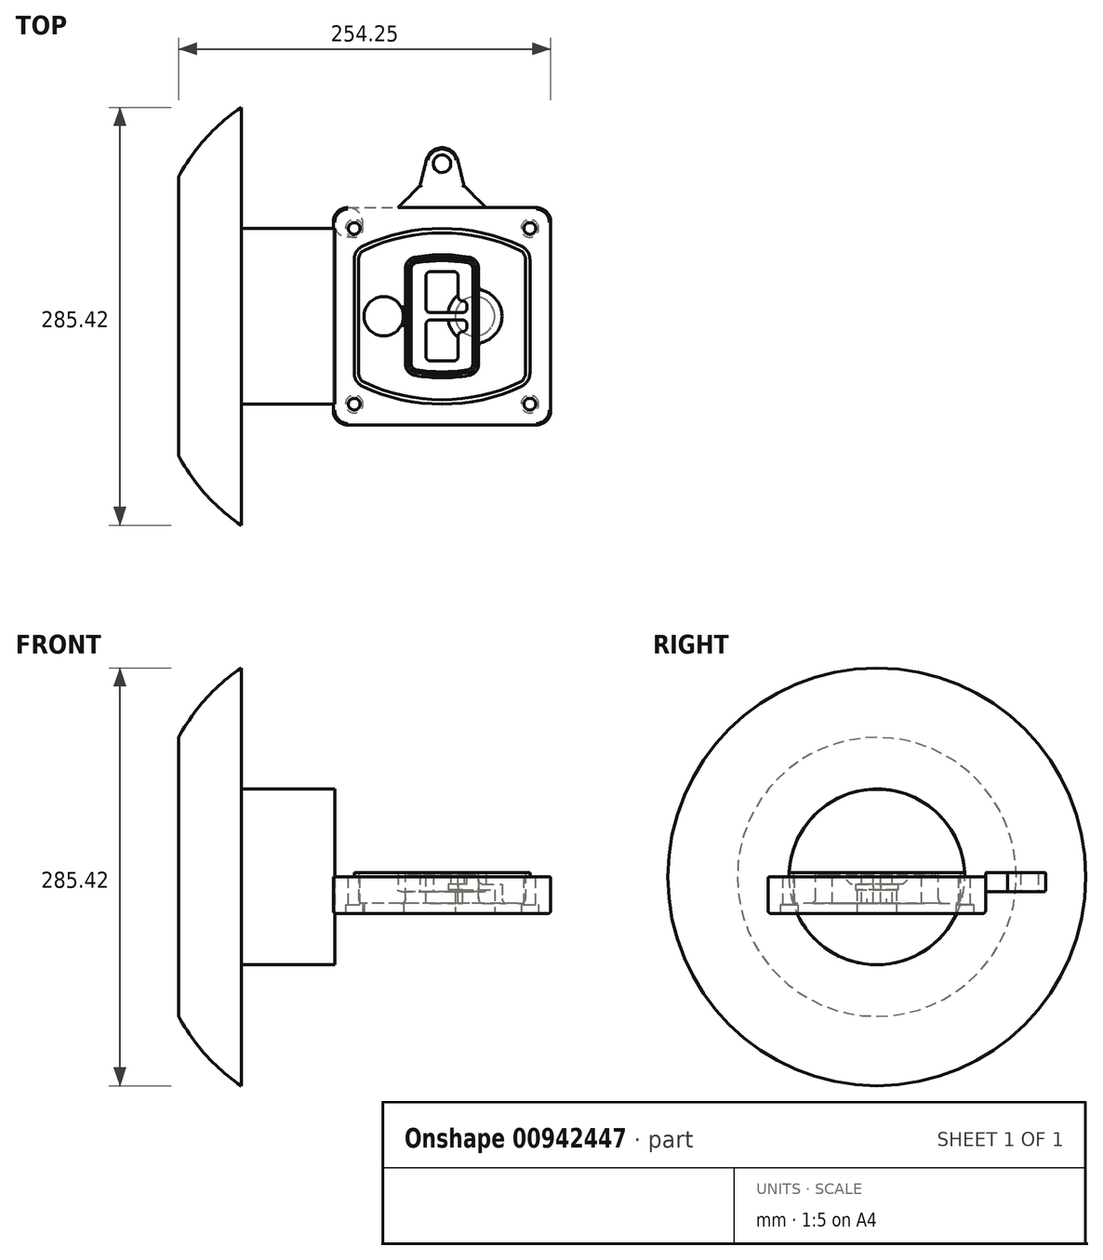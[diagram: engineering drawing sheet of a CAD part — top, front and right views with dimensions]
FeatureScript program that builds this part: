
annotation { "Feature Type Name" : "Feature", "Feature Type Description" : "" }
export const myFeature = defineFeature(function(context is Context, id is Id, definition is map)
    precondition{}
    {
        {
            var Q0;
            Q0=qCreatedBy(makeId("Top.planeOp"),FACE);
            var sketch = newSketch(context, id + "F0", { "sketchPlane" : qUnion([Q0])});
            skPoint(sketch, "E0.rect.middle", {"position": v(0, 0) * mm});
            skLineSegment(sketch, "E1.bottom", {"start": v(-64.25, -74.25) * mm, "end": v(64.25, -74.25) * mm});
            skLineSegment(sketch, "E1.top", {"start": v(-64.25, 74.25) * mm, "end": v(64.25, 74.25) * mm});
            skLineSegment(sketch, "E1.left", {"start": v(-74.25, -64.25) * mm, "end": v(-74.25, 64.25) * mm});
            skLineSegment(sketch, "E1.right", {"start": v(74.25, -64.25) * mm, "end": v(74.25, 64.25) * mm});
            skLineSegment(sketch, "E2", {"start": v(-74.25, 74.25) * mm, "end": v(74.25, -74.25) * mm, "construction": true});
            skLineSegment(sketch, "E3", {"start": v(74.25, 74.25) * mm, "end": v(-74.25, -74.25) * mm, "construction": true});
            skCircle(sketch, "E4", {"center": v(-60, 60) * mm, "radius": 4 * mm});
            skCircle(sketch, "E5", {"center": v(60, 60) * mm, "radius": 4 * mm});
            skCircle(sketch, "E6", {"center": v(60, -60) * mm, "radius": 4 * mm});
            skCircle(sketch, "E7", {"center": v(-60, -60) * mm, "radius": 4 * mm});
            skLineSegment(sketch, "E8", {"start": v(-60, 60) * mm, "end": v(60, 60) * mm, "construction": true});
            skLineSegment(sketch, "E9", {"start": v(60, 60) * mm, "end": v(60, -60) * mm, "construction": true});
            skLineSegment(sketch, "E10", {"start": v(60, -60) * mm, "end": v(-60, -60) * mm, "construction": true});
            skLineSegment(sketch, "E11", {"start": v(-60, -60) * mm, "end": v(-60, 60) * mm, "construction": true});
            skLineSegment(sketch, "E12", {"start": v(-60, 38.83) * mm, "end": v(-60, -38.83) * mm});
            skLineSegment(sketch, "E13", {"start": v(60, 38.83) * mm, "end": v(60, -38.83) * mm});
            skArc(sketch, "E14", {"start": v(54.26, 47.88) * mm, "mid": v(0, 60) * mm, "end": v(-54.26, 47.88) * mm});
            skArc(sketch, "E15", {"start": v(-54.26, -47.88) * mm, "mid": v(0, -60) * mm, "end": v(54.26, -47.88) * mm});
            skLineSegment(sketch, "E16", {"start": v(-60, 0) * mm, "end": v(60, 0) * mm, "construction": true});
            skPoint(sketch, "E17.visualSharp", {"position": v(-60, -45) * mm});
            skArc(sketch, "E17.filletArc", {"start": v(-60, -38.83) * mm, "mid": v(-58.44, -44.2) * mm, "end": v(-54.26, -47.88) * mm});
            skPoint(sketch, "E18.visualSharp", {"position": v(-60, 45) * mm});
            skArc(sketch, "E18.filletArc", {"start": v(-54.26, 47.88) * mm, "mid": v(-58.44, 44.2) * mm, "end": v(-60, 38.83) * mm});
            skPoint(sketch, "E19.visualSharp", {"position": v(60, 45) * mm});
            skArc(sketch, "E19.filletArc", {"start": v(60, 38.83) * mm, "mid": v(58.44, 44.2) * mm, "end": v(54.26, 47.88) * mm});
            skPoint(sketch, "E20.visualSharp", {"position": v(60, -45) * mm});
            skArc(sketch, "E20.filletArc", {"start": v(54.26, -47.88) * mm, "mid": v(58.44, -44.2) * mm, "end": v(60, -38.83) * mm});
            skPoint(sketch, "E21.visualSharp", {"position": v(-74.25, 74.25) * mm});
            skArc(sketch, "E21.filletArc", {"start": v(-64.25, 74.25) * mm, "mid": v(-71.32, 71.32) * mm, "end": v(-74.25, 64.25) * mm});
            skPoint(sketch, "E22.visualSharp", {"position": v(74.25, 74.25) * mm});
            skArc(sketch, "E22.filletArc", {"start": v(74.25, 64.25) * mm, "mid": v(71.32, 71.32) * mm, "end": v(64.25, 74.25) * mm});
            skPoint(sketch, "E23.visualSharp", {"position": v(74.25, -74.25) * mm});
            skArc(sketch, "E23.filletArc", {"start": v(64.25, -74.25) * mm, "mid": v(71.32, -71.32) * mm, "end": v(74.25, -64.25) * mm});
            skPoint(sketch, "E24.visualSharp", {"position": v(-74.25, -74.25) * mm});
            skArc(sketch, "E24.filletArc", {"start": v(-74.25, -64.25) * mm, "mid": v(-71.32, -71.32) * mm, "end": v(-64.25, -74.25) * mm});
            skArc(sketch, "E25.0", {"start": v(57, 38.83) * mm, "mid": v(55.9, 42.58) * mm, "end": v(52.98, 45.17) * mm});
            skLineSegment(sketch, "E25.1", {"start": v(57, 38.83) * mm, "end": v(57, -38.83) * mm});
            skArc(sketch, "E25.2", {"start": v(52.98, -45.17) * mm, "mid": v(55.9, -42.58) * mm, "end": v(57, -38.83) * mm});
            skArc(sketch, "E25.3", {"start": v(-52.98, -45.17) * mm, "mid": v(0, -57) * mm, "end": v(52.98, -45.17) * mm});
            skArc(sketch, "E25.4", {"start": v(-57, -38.83) * mm, "mid": v(-55.9, -42.58) * mm, "end": v(-52.98, -45.17) * mm});
            skArc(sketch, "E25.5", {"start": v(52.98, 45.17) * mm, "mid": v(0, 57) * mm, "end": v(-52.98, 45.17) * mm});
            skLineSegment(sketch, "E25.6", {"start": v(-57, 38.83) * mm, "end": v(-57, -38.83) * mm});
            skArc(sketch, "E25.7", {"start": v(-52.98, 45.17) * mm, "mid": v(-55.9, 42.58) * mm, "end": v(-57, 38.83) * mm});
            skArc(sketch, "E26.0", {"start": v(-55.96, 51.5) * mm, "mid": v(-61.82, 46.33) * mm, "end": v(-64, 38.83) * mm});
            skArc(sketch, "E26.1", {"start": v(55.96, 51.5) * mm, "mid": v(0, 64) * mm, "end": v(-55.96, 51.5) * mm});
            skArc(sketch, "E26.2", {"start": v(64, 38.83) * mm, "mid": v(61.82, 46.33) * mm, "end": v(55.96, 51.5) * mm});
            skLineSegment(sketch, "E26.3", {"start": v(64, 38.83) * mm, "end": v(64, -38.83) * mm});
            skArc(sketch, "E26.4", {"start": v(55.96, -51.5) * mm, "mid": v(61.82, -46.33) * mm, "end": v(64, -38.83) * mm});
            skLineSegment(sketch, "E26.5", {"start": v(-64, 38.83) * mm, "end": v(-64, -38.83) * mm});
            skArc(sketch, "E26.6", {"start": v(-55.96, -51.5) * mm, "mid": v(0, -64) * mm, "end": v(55.96, -51.5) * mm});
            skArc(sketch, "E26.7", {"start": v(-64, -38.83) * mm, "mid": v(-61.82, -46.33) * mm, "end": v(-55.96, -51.5) * mm});
            skSolve(sketch);
        }
        {
            var Q0;
            Q0=makeQuery(id+"F0.imprint","IMPRINT",FACE,{"disambiguationData":[TD([[makeQuery(id+"F0.imprint","IMPRINT",EDGE,{"derivedFrom":sQuery(id+"F0.wireOp",EDGE,"E1.bottom")}),1.0]])]});
            var Q1;
            Q1=makeQuery(id+"F0.imprint","IMPRINT",FACE,{"disambiguationData":[TD([[makeQuery(id+"F0.imprint","IMPRINT",EDGE,{"derivedFrom":sQuery(id+"F0.wireOp",EDGE,"E12")}),1.0]])]});
            var Q2;
            Q2=makeQuery(id+"F0.imprint","IMPRINT",FACE,{"disambiguationData":[TD([[makeQuery(id+"F0.imprint","IMPRINT",EDGE,{"derivedFrom":sQuery(id+"F0.wireOp",EDGE,"E25.0")}),1.0]])]});
            var Q3;
            Q3=makeQuery(id+"F0.imprint","IMPRINT",FACE,{"disambiguationData":[TD([[makeQuery(id+"F0.imprint","IMPRINT",EDGE,{"derivedFrom":sQuery(id+"F0.wireOp",EDGE,"E12")}),-1.0]])]});
            extrude(context, id + "F1", {"entities" : qUnion([Q0, Q1, Q2, Q3]), "oppositeDirection" : true, "depth" : 25 * mm});
        }
        {
            var Q0;
            Q0=makeQuery(id+"F0.imprint","IMPRINT",FACE,{"disambiguationData":[TD([[makeQuery(id+"F0.imprint","IMPRINT",EDGE,{"derivedFrom":sQuery(id+"F0.wireOp",EDGE,"E12")}),1.0]])]});
            extrude(context, id + "F2", {"entities" : qUnion([Q0]), "operationType" : NewBodyOperationType.ADD, "depth" : 3 * mm});
        }
        {
            var Q0;
            Q0=makeQuery(id+"F0.imprint","IMPRINT",FACE,{"disambiguationData":[TD([[makeQuery(id+"F0.imprint","IMPRINT",EDGE,{"derivedFrom":sQuery(id+"F0.wireOp",EDGE,"E25.0")}),1.0]])]});
            extrude(context, id + "F3", {"entities" : qUnion([Q0]), "operationType" : NewBodyOperationType.REMOVE, "oppositeDirection" : true, "depth" : 18 * mm});
        }
        {
            var Q0;
            Q0=makeQuery(id+"F2.opExtrude","CAP_FACE",FACE,{"disambiguationData":[OSD([sQuery(id+"F0.wireOp",EDGE,"E12"),sQuery(id+"F0.wireOp",EDGE,"E13"),sQuery(id+"F0.wireOp",EDGE,"E14"),sQuery(id+"F0.wireOp",EDGE,"E15"),sQuery(id+"F0.wireOp",EDGE,"E17.filletArc"),sQuery(id+"F0.wireOp",EDGE,"E18.filletArc"),sQuery(id+"F0.wireOp",EDGE,"E19.filletArc"),sQuery(id+"F0.wireOp",EDGE,"E20.filletArc"),sQuery(id+"F0.wireOp",EDGE,"E25.0"),sQuery(id+"F0.wireOp",EDGE,"E25.1"),sQuery(id+"F0.wireOp",EDGE,"E25.2"),sQuery(id+"F0.wireOp",EDGE,"E25.3"),sQuery(id+"F0.wireOp",EDGE,"E25.4"),sQuery(id+"F0.wireOp",EDGE,"E25.5"),sQuery(id+"F0.wireOp",EDGE,"E25.6"),sQuery(id+"F0.wireOp",EDGE,"E25.7")])],"isStart":false});
            var sketch = newSketch(context, id + "F4", { "sketchPlane" : qUnion([Q0])});
            skArc(sketch, "E27.0", {"start": v(-18.34, -40.45) * mm, "mid": v(0, -42) * mm, "end": v(18.34, -40.45) * mm});
            skArc(sketch, "E28.0", {"start": v(18.34, 40.45) * mm, "mid": v(0, 42) * mm, "end": v(-18.34, 40.45) * mm});
            skLineSegment(sketch, "E29", {"start": v(-25, 32.57) * mm, "end": v(-25, -32.57) * mm});
            skLineSegment(sketch, "E30", {"start": v(25, 32.57) * mm, "end": v(25, -32.57) * mm});
            skLineSegment(sketch, "E31", {"start": v(-25, 39.1) * mm, "end": v(25, 39.1) * mm, "construction": true});
            skLineSegment(sketch, "E32", {"start": v(-25, -39.1) * mm, "end": v(25, -39.1) * mm, "construction": true});
            skPoint(sketch, "E33.visualSharp", {"position": v(-25, 39.1) * mm});
            skArc(sketch, "E33.filletArc", {"start": v(-18.34, 40.45) * mm, "mid": v(-23.11, 37.73) * mm, "end": v(-25, 32.57) * mm});
            skPoint(sketch, "E34.visualSharp", {"position": v(25, 39.1) * mm});
            skArc(sketch, "E34.filletArc", {"start": v(25, 32.57) * mm, "mid": v(23.11, 37.73) * mm, "end": v(18.34, 40.45) * mm});
            skPoint(sketch, "E35.visualSharp", {"position": v(25, -39.1) * mm});
            skArc(sketch, "E35.filletArc", {"start": v(18.34, -40.45) * mm, "mid": v(23.11, -37.73) * mm, "end": v(25, -32.57) * mm});
            skPoint(sketch, "E36.visualSharp", {"position": v(-25, -39.1) * mm});
            skArc(sketch, "E36.filletArc", {"start": v(-25, -32.57) * mm, "mid": v(-23.11, -37.73) * mm, "end": v(-18.34, -40.45) * mm});
            skArc(sketch, "E37.0", {"start": v(52.98, 45.17) * mm, "mid": v(0, 57) * mm, "end": v(-52.98, 45.17) * mm});
            skArc(sketch, "E37.1", {"start": v(-52.98, 45.17) * mm, "mid": v(-55.9, 42.58) * mm, "end": v(-57, 38.83) * mm});
            skLineSegment(sketch, "E37.2", {"start": v(-57, 38.83) * mm, "end": v(-57, -38.83) * mm});
            skArc(sketch, "E37.3", {"start": v(-57, -38.83) * mm, "mid": v(-55.9, -42.58) * mm, "end": v(-52.98, -45.17) * mm});
            skArc(sketch, "E37.4", {"start": v(-52.98, -45.17) * mm, "mid": v(0, -57) * mm, "end": v(52.98, -45.17) * mm});
            skArc(sketch, "E37.5", {"start": v(52.98, -45.17) * mm, "mid": v(55.9, -42.58) * mm, "end": v(57, -38.83) * mm});
            skLineSegment(sketch, "E37.6", {"start": v(57, 38.83) * mm, "end": v(57, -38.83) * mm});
            skArc(sketch, "E37.7", {"start": v(57, 38.83) * mm, "mid": v(55.9, 42.58) * mm, "end": v(52.98, 45.17) * mm});
            skLineSegment(sketch, "E38.0", {"start": v(23, 32.57) * mm, "end": v(23, -32.57) * mm});
            skArc(sketch, "E38.1", {"start": v(18, -38.48) * mm, "mid": v(21.58, -36.44) * mm, "end": v(23, -32.57) * mm});
            skArc(sketch, "E38.2", {"start": v(-18, -38.48) * mm, "mid": v(0, -40) * mm, "end": v(18, -38.48) * mm});
            skArc(sketch, "E38.3", {"start": v(-23, -32.57) * mm, "mid": v(-21.58, -36.44) * mm, "end": v(-18, -38.48) * mm});
            skLineSegment(sketch, "E38.4", {"start": v(-23, 32.57) * mm, "end": v(-23, -32.57) * mm});
            skArc(sketch, "E38.5", {"start": v(23, 32.57) * mm, "mid": v(21.58, 36.44) * mm, "end": v(18, 38.48) * mm});
            skArc(sketch, "E38.6", {"start": v(-18, 38.48) * mm, "mid": v(-21.58, 36.44) * mm, "end": v(-23, 32.57) * mm});
            skArc(sketch, "E38.7", {"start": v(18, 38.48) * mm, "mid": v(0, 40) * mm, "end": v(-18, 38.48) * mm});
            skArc(sketch, "E39.0", {"start": v(21, 32.57) * mm, "mid": v(20.06, 35.15) * mm, "end": v(17.67, 36.5) * mm});
            skLineSegment(sketch, "E39.1", {"start": v(21, 32.57) * mm, "end": v(21, -32.57) * mm});
            skArc(sketch, "E39.2", {"start": v(17.67, -36.5) * mm, "mid": v(20.06, -35.15) * mm, "end": v(21, -32.57) * mm});
            skArc(sketch, "E39.3", {"start": v(-17.67, -36.5) * mm, "mid": v(0, -38) * mm, "end": v(17.67, -36.5) * mm});
            skArc(sketch, "E39.4", {"start": v(-21, -32.57) * mm, "mid": v(-20.06, -35.15) * mm, "end": v(-17.67, -36.5) * mm});
            skArc(sketch, "E39.5", {"start": v(17.67, 36.5) * mm, "mid": v(0, 38) * mm, "end": v(-17.67, 36.5) * mm});
            skLineSegment(sketch, "E39.6", {"start": v(-21, 32.57) * mm, "end": v(-21, -32.57) * mm});
            skArc(sketch, "E39.7", {"start": v(-17.67, 36.5) * mm, "mid": v(-20.06, 35.15) * mm, "end": v(-21, 32.57) * mm});
            skLineSegment(sketch, "E40", {"start": v(-25, 0) * mm, "end": v(25, 0) * mm, "construction": true});
            skLineSegment(sketch, "E41", {"start": v(-11, 5.5) * mm, "end": v(-11, 27.5) * mm});
            skLineSegment(sketch, "E42", {"start": v(-8, 30.5) * mm, "end": v(8, 30.5) * mm});
            skLineSegment(sketch, "E43", {"start": v(11, 27.5) * mm, "end": v(11, 13.5) * mm});
            skLineSegment(sketch, "E44", {"start": v(14, 10.5) * mm, "end": v(14, 10.5) * mm});
            skLineSegment(sketch, "E45", {"start": v(17, 7.5) * mm, "end": v(17, 5.5) * mm});
            skLineSegment(sketch, "E46", {"start": v(14, 2.5) * mm, "end": v(-8, 2.5) * mm});
            skPoint(sketch, "E47.visualSharp", {"position": v(-11, 30.5) * mm});
            skArc(sketch, "E47.filletArc", {"start": v(-8, 30.5) * mm, "mid": v(-10.12, 29.62) * mm, "end": v(-11, 27.5) * mm});
            skPoint(sketch, "E48.visualSharp", {"position": v(11, 30.5) * mm});
            skArc(sketch, "E48.filletArc", {"start": v(11, 27.5) * mm, "mid": v(10.12, 29.62) * mm, "end": v(8, 30.5) * mm});
            skPoint(sketch, "E49.visualSharp", {"position": v(11, 10.5) * mm});
            skArc(sketch, "E49.filletArc", {"start": v(11, 13.5) * mm, "mid": v(11.88, 11.38) * mm, "end": v(14, 10.5) * mm});
            skPoint(sketch, "E50.visualSharp", {"position": v(17, 10.5) * mm});
            skArc(sketch, "E50.filletArc", {"start": v(17, 7.5) * mm, "mid": v(16.12, 9.62) * mm, "end": v(14, 10.5) * mm});
            skPoint(sketch, "E51.visualSharp", {"position": v(17, 2.5) * mm});
            skArc(sketch, "E51.filletArc", {"start": v(14, 2.5) * mm, "mid": v(16.12, 3.38) * mm, "end": v(17, 5.5) * mm});
            skPoint(sketch, "E52.visualSharp", {"position": v(-11, 2.5) * mm});
            skArc(sketch, "E52.filletArc", {"start": v(-11, 5.5) * mm, "mid": v(-10.12, 3.38) * mm, "end": v(-8, 2.5) * mm});
            skLineSegment(sketch, "E53.0.MirrorCS", {"start": v(14, -2.5) * mm, "end": v(-8, -2.5) * mm});
            skArc(sketch, "E54.0.MirrorCS", {"start": v(-11, -5.5) * mm, "mid": v(-10.12, -3.38) * mm, "end": v(-8, -2.5) * mm});
            skLineSegment(sketch, "E55.0.MirrorCS", {"start": v(-11, -5.5) * mm, "end": v(-11, -27.5) * mm});
            skArc(sketch, "E56.0.MirrorCS", {"start": v(-8, -30.5) * mm, "mid": v(-10.12, -29.62) * mm, "end": v(-11, -27.5) * mm});
            skLineSegment(sketch, "E57.0.MirrorCS", {"start": v(-8, -30.5) * mm, "end": v(8, -30.5) * mm});
            skArc(sketch, "E58.0.MirrorCS", {"start": v(11, -27.5) * mm, "mid": v(10.12, -29.62) * mm, "end": v(8, -30.5) * mm});
            skLineSegment(sketch, "E59.0.MirrorCS", {"start": v(11, -27.5) * mm, "end": v(11, -13.5) * mm});
            skArc(sketch, "E60.0.MirrorCS", {"start": v(11, -13.5) * mm, "mid": v(11.88, -11.38) * mm, "end": v(14, -10.5) * mm});
            skArc(sketch, "E61.0.MirrorCS", {"start": v(17, -7.5) * mm, "mid": v(16.12, -9.62) * mm, "end": v(14, -10.5) * mm});
            skLineSegment(sketch, "E62.0.MirrorCS", {"start": v(17, -7.5) * mm, "end": v(17, -5.5) * mm});
            skArc(sketch, "E63.0.MirrorCS", {"start": v(14, -2.5) * mm, "mid": v(16.12, -3.38) * mm, "end": v(17, -5.5) * mm});
            skSolve(sketch);
        }
        {
            var Q0;
            Q0=makeQuery(id+"F4.imprint","IMPRINT",FACE,{"disambiguationData":[TD([[makeQuery(id+"F4.imprint","IMPRINT",EDGE,{"derivedFrom":sQuery(id+"F4.wireOp",EDGE,"E27.0")}),1.0]])]});
            var Q1;
            Q1=makeQuery(id+"F4.imprint","IMPRINT",FACE,{"disambiguationData":[TD([[makeQuery(id+"F4.imprint","IMPRINT",EDGE,{"derivedFrom":sQuery(id+"F4.wireOp",EDGE,"E38.0")}),-1.0]])]});
            var Q2;
            Q2=makeQuery(id+"F4.imprint","IMPRINT",FACE,{"disambiguationData":[TD([[makeQuery(id+"F4.imprint","IMPRINT",EDGE,{"derivedFrom":sQuery(id+"F4.wireOp",EDGE,"E39.0")}),1.0]])]});
            extrude(context, id + "F5", {"entities" : qUnion([Q0, Q1, Q2]), "operationType" : NewBodyOperationType.ADD, "endBound" : BoundingType.UP_TO_NEXT, "oppositeDirection" : true, "depth" : 25 * mm});
        }
        {
            var Q0;
            Q0=makeQuery(id+"F4.imprint","IMPRINT",FACE,{"disambiguationData":[TD([[makeQuery(id+"F4.imprint","IMPRINT",EDGE,{"derivedFrom":sQuery(id+"F4.wireOp",EDGE,"E38.0")}),-1.0]])]});
            extrude(context, id + "F6", {"entities" : qUnion([Q0]), "operationType" : NewBodyOperationType.REMOVE, "oppositeDirection" : true, "depth" : 2 * mm});
        }
        {
            var Q0;
            Q0=makeQuery(id+"F1.opExtrude","CAP_FACE",FACE,{"disambiguationData":[OSD([sQuery(id+"F0.wireOp",EDGE,"E1.bottom"),sQuery(id+"F0.wireOp",EDGE,"E1.top"),sQuery(id+"F0.wireOp",EDGE,"E1.left"),sQuery(id+"F0.wireOp",EDGE,"E1.right"),sQuery(id+"F0.wireOp",EDGE,"E4"),sQuery(id+"F0.wireOp",EDGE,"E5"),sQuery(id+"F0.wireOp",EDGE,"E6"),sQuery(id+"F0.wireOp",EDGE,"E7"),sQuery(id+"F0.wireOp",EDGE,"E21.filletArc"),sQuery(id+"F0.wireOp",EDGE,"E22.filletArc"),sQuery(id+"F0.wireOp",EDGE,"E23.filletArc"),sQuery(id+"F0.wireOp",EDGE,"E24.filletArc")])],"isStart":false});
            var sketch = newSketch(context, id + "F7", { "sketchPlane" : qUnion([Q0])});
            skCircle(sketch, "E64", {"center": v(22.5, 0) * mm, "radius": 13.47 * mm});
            skCircle(sketch, "E65", {"center": v(-39.81, 0) * mm, "radius": 13.47 * mm});
            skLineSegment(sketch, "E66", {"start": v(74.25, 0) * mm, "end": v(-74.25, 0) * mm});
            skCircle(sketch, "E67", {"center": v(22.5, 0) * mm, "radius": 18.47 * mm});
            skCircle(sketch, "E68", {"center": v(60, -60) * mm, "radius": 6 * mm});
            skCircle(sketch, "E69", {"center": v(-60, -60) * mm, "radius": 6 * mm});
            skCircle(sketch, "E70", {"center": v(-60, 60) * mm, "radius": 6 * mm});
            skCircle(sketch, "E71", {"center": v(60, 60) * mm, "radius": 6 * mm});
            skSolve(sketch);
        }
        {
            var Q0;
            {var subQ1=sQuery(id+"F7.wireOp",EDGE,"E66");var subQ4=sQuery(id+"F7.wireOp",EDGE,"E64");var subQ6=makeQuery(id+"F7.imprint","INTERSECT",VERTEX,{"disambiguationData":[OD(0.0)],"derivedFrom":[subQ4,subQ1]});Q0=makeQuery(id+"F7.imprint","IMPRINT",FACE,{"disambiguationData":[TD([[makeQuery(id+"F7.imprint","IMPRINT",EDGE,{"disambiguationData":[TD([[subQ6,-1.0]])],"derivedFrom":subQ4}),-1.0]])]});}
            var Q1;
            {var subQ0=sQuery(id+"F7.wireOp",EDGE,"E66");var subQ1=sQuery(id+"F7.wireOp",EDGE,"E64");var subQ3=makeQuery(id+"F7.imprint","INTERSECT",VERTEX,{"disambiguationData":[OD(0.0)],"derivedFrom":[subQ1,subQ0]});Q1=makeQuery(id+"F7.imprint","IMPRINT",FACE,{"disambiguationData":[TD([[makeQuery(id+"F7.imprint","IMPRINT",EDGE,{"disambiguationData":[TD([[subQ3,-1.0]])],"derivedFrom":subQ1}),1.0]])]});}
            var Q2;
            {var subQ0=sQuery(id+"F7.wireOp",EDGE,"E66");var subQ1=sQuery(id+"F7.wireOp",EDGE,"E64");var subQ3=makeQuery(id+"F7.imprint","INTERSECT",VERTEX,{"disambiguationData":[OD(0.0)],"derivedFrom":[subQ1,subQ0]});Q2=makeQuery(id+"F7.imprint","IMPRINT",FACE,{"disambiguationData":[TD([[makeQuery(id+"F7.imprint","IMPRINT",EDGE,{"disambiguationData":[TD([[subQ3,1.0]])],"derivedFrom":subQ1}),1.0]])]});}
            var Q3;
            {var subQ1=sQuery(id+"F7.wireOp",EDGE,"E66");var subQ4=sQuery(id+"F7.wireOp",EDGE,"E64");var subQ6=makeQuery(id+"F7.imprint","INTERSECT",VERTEX,{"disambiguationData":[OD(0.0)],"derivedFrom":[subQ4,subQ1]});Q3=makeQuery(id+"F7.imprint","IMPRINT",FACE,{"disambiguationData":[TD([[makeQuery(id+"F7.imprint","IMPRINT",EDGE,{"disambiguationData":[TD([[subQ6,1.0]])],"derivedFrom":subQ4}),-1.0]])]});}
            extrude(context, id + "F8", {"entities" : qUnion([Q0, Q1, Q2, Q3]), "operationType" : NewBodyOperationType.ADD, "oppositeDirection" : true, "depth" : 20 * mm});
        }
        {
            var Q0;
            {var subQ0=sQuery(id+"F7.wireOp",EDGE,"E66");var subQ1=sQuery(id+"F7.wireOp",EDGE,"E64");var subQ3=makeQuery(id+"F7.imprint","INTERSECT",VERTEX,{"disambiguationData":[OD(0.0)],"derivedFrom":[subQ1,subQ0]});Q0=makeQuery(id+"F7.imprint","IMPRINT",FACE,{"disambiguationData":[TD([[makeQuery(id+"F7.imprint","IMPRINT",EDGE,{"disambiguationData":[TD([[subQ3,-1.0]])],"derivedFrom":subQ1}),1.0]])]});}
            var Q1;
            {var subQ0=sQuery(id+"F7.wireOp",EDGE,"E66");var subQ1=sQuery(id+"F7.wireOp",EDGE,"E64");var subQ3=makeQuery(id+"F7.imprint","INTERSECT",VERTEX,{"disambiguationData":[OD(0.0)],"derivedFrom":[subQ1,subQ0]});Q1=makeQuery(id+"F7.imprint","IMPRINT",FACE,{"disambiguationData":[TD([[makeQuery(id+"F7.imprint","IMPRINT",EDGE,{"disambiguationData":[TD([[subQ3,1.0]])],"derivedFrom":subQ1}),1.0]])]});}
            extrude(context, id + "F9", {"entities" : qUnion([Q0, Q1]), "operationType" : NewBodyOperationType.REMOVE, "oppositeDirection" : true, "depth" : 16 * mm});
        }
        {
            var Q0;
            {var subQ0=sQuery(id+"F7.wireOp",EDGE,"E66");var subQ1=sQuery(id+"F7.wireOp",EDGE,"E65");var subQ3=makeQuery(id+"F7.imprint","INTERSECT",VERTEX,{"disambiguationData":[OD(0.0)],"derivedFrom":[subQ1,subQ0]});Q0=makeQuery(id+"F7.imprint","IMPRINT",FACE,{"disambiguationData":[TD([[makeQuery(id+"F7.imprint","IMPRINT",EDGE,{"disambiguationData":[TD([[subQ3,-1.0]])],"derivedFrom":subQ1}),1.0]])]});}
            var Q1;
            {var subQ0=sQuery(id+"F7.wireOp",EDGE,"E66");var subQ1=sQuery(id+"F7.wireOp",EDGE,"E65");var subQ3=makeQuery(id+"F7.imprint","INTERSECT",VERTEX,{"disambiguationData":[OD(0.0)],"derivedFrom":[subQ1,subQ0]});Q1=makeQuery(id+"F7.imprint","IMPRINT",FACE,{"disambiguationData":[TD([[makeQuery(id+"F7.imprint","IMPRINT",EDGE,{"disambiguationData":[TD([[subQ3,1.0]])],"derivedFrom":subQ1}),1.0]])]});}
            extrude(context, id + "F10", {"entities" : qUnion([Q0, Q1]), "operationType" : NewBodyOperationType.REMOVE, "oppositeDirection" : true, "depth" : 25 * mm});
        }
        {
            var Q0;
            Q0=makeQuery(id+"F7.imprint","IMPRINT",FACE,{"disambiguationData":[TD([[makeQuery(id+"F7.imprint","IMPRINT",EDGE,{"derivedFrom":sQuery(id+"F7.wireOp",EDGE,"E68")}),1.0]])]});
            var Q1;
            Q1=makeQuery(id+"F7.imprint","IMPRINT",FACE,{"disambiguationData":[TD([[makeQuery(id+"F7.imprint","IMPRINT",EDGE,{"derivedFrom":makeQuery(id+"F1.opExtrude","CAP_EDGE",EDGE,{"disambiguationData":[OSD([sQuery(id+"F0.wireOp",EDGE,"E5")])],"isStart":false})}),-1.0]])]});
            var Q2;
            Q2=makeQuery(id+"F7.imprint","IMPRINT",FACE,{"disambiguationData":[TD([[makeQuery(id+"F7.imprint","IMPRINT",EDGE,{"derivedFrom":sQuery(id+"F7.wireOp",EDGE,"E69")}),1.0]])]});
            var Q3;
            Q3=makeQuery(id+"F7.imprint","IMPRINT",FACE,{"disambiguationData":[TD([[makeQuery(id+"F7.imprint","IMPRINT",EDGE,{"derivedFrom":makeQuery(id+"F1.opExtrude","CAP_EDGE",EDGE,{"disambiguationData":[OSD([sQuery(id+"F0.wireOp",EDGE,"E4")])],"isStart":false})}),-1.0]])]});
            var Q4;
            Q4=makeQuery(id+"F7.imprint","IMPRINT",FACE,{"disambiguationData":[TD([[makeQuery(id+"F7.imprint","IMPRINT",EDGE,{"derivedFrom":sQuery(id+"F7.wireOp",EDGE,"E70")}),1.0]])]});
            var Q5;
            Q5=makeQuery(id+"F7.imprint","IMPRINT",FACE,{"disambiguationData":[TD([[makeQuery(id+"F7.imprint","IMPRINT",EDGE,{"derivedFrom":makeQuery(id+"F1.opExtrude","CAP_EDGE",EDGE,{"disambiguationData":[OSD([sQuery(id+"F0.wireOp",EDGE,"E7")])],"isStart":false})}),-1.0]])]});
            var Q6;
            Q6=makeQuery(id+"F7.imprint","IMPRINT",FACE,{"disambiguationData":[TD([[makeQuery(id+"F7.imprint","IMPRINT",EDGE,{"derivedFrom":sQuery(id+"F7.wireOp",EDGE,"E71")}),1.0]])]});
            var Q7;
            Q7=makeQuery(id+"F7.imprint","IMPRINT",FACE,{"disambiguationData":[TD([[makeQuery(id+"F7.imprint","IMPRINT",EDGE,{"derivedFrom":makeQuery(id+"F1.opExtrude","CAP_EDGE",EDGE,{"disambiguationData":[OSD([sQuery(id+"F0.wireOp",EDGE,"E6")])],"isStart":false})}),-1.0]])]});
            extrude(context, id + "F11", {"entities" : qUnion([Q0, Q1, Q2, Q3, Q4, Q5, Q6, Q7]), "operationType" : NewBodyOperationType.REMOVE, "oppositeDirection" : true, "depth" : 6 * mm});
        }
        {
            var Q0;
            Q0=makeQuery(id+"F9.boolean.opBoolean","COPY",FACE,{"derivedFrom":makeQuery(id+"F9.opExtrude","CAP_FACE",FACE,{"disambiguationData":[OSD([sQuery(id+"F7.wireOp",EDGE,"E64")])],"isStart":false})});
            var sketch = newSketch(context, id + "F12", { "sketchPlane" : qUnion([Q0])});
            skArc(sketch, "E72.0", {"start": v(11, 14.45) * mm, "mid": v(6.45, 9.13) * mm, "end": v(4.2, 2.5) * mm});
            skArc(sketch, "E72.1", {"start": v(4.2, -2.5) * mm, "mid": v(6.45, -9.13) * mm, "end": v(11, -14.45) * mm});
            skLineSegment(sketch, "E73", {"start": v(4.2, -2.5) * mm, "end": v(14, -2.5) * mm});
            skLineSegment(sketch, "E74.0", {"start": v(14, 2.5) * mm, "end": v(4.2, 2.5) * mm});
            skArc(sketch, "E74.1", {"start": v(14, 2.5) * mm, "mid": v(16.12, 3.38) * mm, "end": v(17, 5.5) * mm});
            skLineSegment(sketch, "E74.2", {"start": v(17, 7.5) * mm, "end": v(17, 5.5) * mm});
            skArc(sketch, "E74.3", {"start": v(17, 7.5) * mm, "mid": v(16.12, 9.62) * mm, "end": v(14, 10.5) * mm});
            skArc(sketch, "E74.4", {"start": v(11, 13.5) * mm, "mid": v(11.88, 11.38) * mm, "end": v(14, 10.5) * mm});
            skLineSegment(sketch, "E74.5", {"start": v(11, 14.45) * mm, "end": v(11, 13.5) * mm});
            skLineSegment(sketch, "E74.7", {"start": v(14, -2.5) * mm, "end": v(4.2, -2.5) * mm});
            skArc(sketch, "E74.8", {"start": v(14, -2.5) * mm, "mid": v(16.12, -3.38) * mm, "end": v(17, -5.5) * mm});
            skLineSegment(sketch, "E74.9", {"start": v(17, -7.5) * mm, "end": v(17, -5.5) * mm});
            skArc(sketch, "E74.10", {"start": v(17, -7.5) * mm, "mid": v(16.12, -9.62) * mm, "end": v(14, -10.5) * mm});
            skArc(sketch, "E74.11", {"start": v(11, -13.5) * mm, "mid": v(11.88, -11.38) * mm, "end": v(14, -10.5) * mm});
            skLineSegment(sketch, "E74.12", {"start": v(11, -14.45) * mm, "end": v(11, -13.5) * mm});
            skPoint(sketch, "E75.orphan", {"position": v(11, -27.5) * mm});
            skPoint(sketch, "E76.orphan", {"position": v(-8, -2.5) * mm});
            skPoint(sketch, "E77.orphan", {"position": v(-8, 2.5) * mm});
            skPoint(sketch, "E78.orphan", {"position": v(11, 27.5) * mm});
            skSolve(sketch);
        }
        {
            var Q0;
            {var subQ7=sQuery(id+"F12.wireOp",EDGE,"E72.0");var subQ14=sQuery(id+"F12.wireOp",EDGE,"E72.1");var subQ16=sQuery(id+"F12.wireOp",EDGE,"E74.1");var subQ18=sQuery(id+"F12.wireOp",EDGE,"E74.8");Q0=qUnion([makeQuery(id+"F12.imprint","IMPRINT",FACE,{"disambiguationData":[TD([[makeQuery(id+"F12.imprint","IMPRINT",EDGE,{"derivedFrom":subQ7}),1.0]])]}),makeQuery(id+"F12.imprint","IMPRINT",FACE,{"disambiguationData":[TD([[makeQuery(id+"F12.imprint","IMPRINT",EDGE,{"derivedFrom":subQ14}),1.0]])]}),makeQuery(id+"F12.imprint","IMPRINT",FACE,{"disambiguationData":[TD([[makeQuery(id+"F12.imprint","IMPRINT",EDGE,{"derivedFrom":subQ16}),1.0]])]}),makeQuery(id+"F12.imprint","IMPRINT",FACE,{"disambiguationData":[TD([[makeQuery(id+"F12.imprint","IMPRINT",EDGE,{"derivedFrom":subQ18}),-1.0]])]})]);}
            var Q1;
            Q1=makeQuery(id+"F5.boolean.opBoolean","SPLIT",FACE,{"disambiguationData":[TD([makeQuery(id+"F5.opExtrude","SWEPT_FACE",FACE,{"disambiguationData":[OSD([sQuery(id+"F4.wireOp",EDGE,"E41")])]})])],"derivedFrom":makeQuery(id+"F3.boolean.opBoolean","COPY",FACE,{"derivedFrom":makeQuery(id+"F3.opExtrude","CAP_FACE",FACE,{"disambiguationData":[OSD([sQuery(id+"F0.wireOp",EDGE,"E25.0"),sQuery(id+"F0.wireOp",EDGE,"E25.1"),sQuery(id+"F0.wireOp",EDGE,"E25.2"),sQuery(id+"F0.wireOp",EDGE,"E25.3"),sQuery(id+"F0.wireOp",EDGE,"E25.4"),sQuery(id+"F0.wireOp",EDGE,"E25.5"),sQuery(id+"F0.wireOp",EDGE,"E25.6"),sQuery(id+"F0.wireOp",EDGE,"E25.7")])],"isStart":false})})});
            extrude(context, id + "F13", {"entities" : qUnion([Q0]), "operationType" : NewBodyOperationType.REMOVE, "endBound" : BoundingType.UP_TO_SURFACE, "endBoundEntityFace" : qUnion([Q1]), "depth" : 25 * mm});
        }
        {
            var Q0;
            Q0=makeQuery(id+"F3.boolean.opBoolean","COPY",EDGE,{"derivedFrom":makeQuery(id+"F3.opExtrude","CAP_EDGE",EDGE,{"disambiguationData":[OSD([sQuery(id+"F0.wireOp",EDGE,"E25.6")])],"isStart":false})});
            var Q1;
            Q1=makeQuery(id+"F8.boolean.opBoolean","INTERSECT",EDGE,{"derivedFrom":[makeQuery(id+"F5.opExtrude","SWEPT_FACE",FACE,{"disambiguationData":[OSD([sQuery(id+"F4.wireOp",EDGE,"E30")])]}),makeQuery(id+"F8.opExtrude","CAP_FACE",FACE,{"disambiguationData":[OSD([sQuery(id+"F7.wireOp",EDGE,"E67")])],"isStart":false})]});
            var Q2;
            Q2=makeQuery(id+"F8.boolean.opBoolean","INTERSECT",EDGE,{"disambiguationData":[OD(1.0)],"derivedFrom":[makeQuery(id+"F5.opExtrude","SWEPT_FACE",FACE,{"disambiguationData":[OSD([sQuery(id+"F4.wireOp",EDGE,"E30")])]}),makeQuery(id+"F8.opExtrude","SWEPT_FACE",FACE,{"disambiguationData":[OSD([sQuery(id+"F7.wireOp",EDGE,"E67")])]})]});
            var Q3;
            {var subQ0=sQuery(id+"F4.wireOp",EDGE,"E30");Q3=makeQuery(id+"F8.boolean.opBoolean","SPLIT",EDGE,{"disambiguationData":[TD([makeQuery(id+"F5.opExtrude","SWEPT_FACE",FACE,{"disambiguationData":[OSD([sQuery(id+"F4.wireOp",EDGE,"E35.filletArc")])]})])],"derivedFrom":makeQuery(id+"F5.opExtrude","CAP_EDGE",EDGE,{"disambiguationData":[OSD([subQ0])],"isStart":false})});}
            var Q4;
            {var subQ0=sQuery(id+"F0.wireOp",EDGE,"E25.7");var subQ1=sQuery(id+"F0.wireOp",EDGE,"E25.1");var subQ2=sQuery(id+"F0.wireOp",EDGE,"E25.6");var subQ3=sQuery(id+"F0.wireOp",EDGE,"E25.5");var subQ4=sQuery(id+"F0.wireOp",EDGE,"E25.4");var subQ5=sQuery(id+"F0.wireOp",EDGE,"E25.0");var subQ6=sQuery(id+"F0.wireOp",EDGE,"E25.2");var subQ7=sQuery(id+"F0.wireOp",EDGE,"E25.3");Q4=makeQuery(id+"F8.boolean.opBoolean","INTERSECT",EDGE,{"derivedFrom":[makeQuery(id+"F5.boolean.opBoolean","SPLIT",FACE,{"disambiguationData":[TD([makeQuery(id+"F2.opExtrude","SWEPT_FACE",FACE,{"disambiguationData":[OSD([subQ5])]})])],"derivedFrom":makeQuery(id+"F3.boolean.opBoolean","COPY",FACE,{"derivedFrom":makeQuery(id+"F3.opExtrude","CAP_FACE",FACE,{"disambiguationData":[OSD([subQ5,subQ1,subQ6,subQ7,subQ4,subQ3,subQ2,subQ0])],"isStart":false})})}),makeQuery(id+"F8.opExtrude","SWEPT_FACE",FACE,{"disambiguationData":[OSD([sQuery(id+"F7.wireOp",EDGE,"E67")])]})]});}
            var Q5;
            Q5=makeQuery(id+"F8.boolean.opBoolean","INTERSECT",EDGE,{"disambiguationData":[OD(0.0)],"derivedFrom":[makeQuery(id+"F5.opExtrude","SWEPT_FACE",FACE,{"disambiguationData":[OSD([sQuery(id+"F4.wireOp",EDGE,"E30")])]}),makeQuery(id+"F8.opExtrude","SWEPT_FACE",FACE,{"disambiguationData":[OSD([sQuery(id+"F7.wireOp",EDGE,"E67")])]})]});
            fillet(context, id + "F14", {"entities" : qUnion([Q0, Q1, Q2, Q3, Q4, Q5]), "radius" : 3 * mm, "tangentPropagation" : true, "allowEdgeOverflow" : false});
        }
        {
            var Q0;
            Q0=makeQuery(id+"F1.opExtrude","CAP_EDGE",EDGE,{"disambiguationData":[OSD([sQuery(id+"F0.wireOp",EDGE,"E1.bottom")])],"isStart":false});
            fillet(context, id + "F15", {"entities" : qUnion([Q0]), "radius" : 2 * mm, "tangentPropagation" : true, "allowEdgeOverflow" : false});
        }
        {
            var Q0;
            {var subQ0=sQuery(id+"F0.wireOp",EDGE,"E21.filletArc");var subQ1=sQuery(id+"F0.wireOp",EDGE,"E7");var subQ2=sQuery(id+"F0.wireOp",EDGE,"E6");var subQ3=sQuery(id+"F0.wireOp",EDGE,"E5");var subQ4=sQuery(id+"F0.wireOp",EDGE,"E4");var subQ5=sQuery(id+"F0.wireOp",EDGE,"E22.filletArc");var subQ6=sQuery(id+"F0.wireOp",EDGE,"E1.bottom");var subQ7=sQuery(id+"F0.wireOp",EDGE,"E1.right");var subQ8=sQuery(id+"F0.wireOp",EDGE,"E1.top");var subQ9=sQuery(id+"F0.wireOp",EDGE,"E1.left");var subQ10=sQuery(id+"F0.wireOp",EDGE,"E23.filletArc");var subQ11=sQuery(id+"F0.wireOp",EDGE,"E24.filletArc");Q0=makeQuery(id+"F2.boolean.opBoolean","SPLIT",FACE,{"disambiguationData":[TD([makeQuery(id+"F1.opExtrude","SWEPT_FACE",FACE,{"disambiguationData":[OSD([subQ6])]})])],"derivedFrom":makeQuery(id+"F1.opExtrude","CAP_FACE",FACE,{"disambiguationData":[OSD([subQ6,subQ8,subQ9,subQ7,subQ4,subQ3,subQ2,subQ1,subQ0,subQ5,subQ10,subQ11])],"isStart":true})});}
            var sketch = newSketch(context, id + "F16", { "sketchPlane" : qUnion([Q0])});
            skLineSegment(sketch, "E79.0", {"start": v(-64.25, 74.25) * mm, "end": v(64.25, 74.25) * mm});
            skArc(sketch, "E79.1", {"start": v(-64.25, 74.25) * mm, "mid": v(-71.32, 71.32) * mm, "end": v(-74.25, 64.25) * mm});
            skLineSegment(sketch, "E79.2", {"start": v(-74.25, -64.25) * mm, "end": v(-74.25, 64.25) * mm});
            skArc(sketch, "E79.3", {"start": v(74.25, 64.25) * mm, "mid": v(71.32, 71.32) * mm, "end": v(64.25, 74.25) * mm});
            skLineSegment(sketch, "E79.4", {"start": v(74.25, -64.25) * mm, "end": v(74.25, 64.25) * mm});
            skArc(sketch, "E79.5", {"start": v(64.25, -74.25) * mm, "mid": v(71.32, -71.32) * mm, "end": v(74.25, -64.25) * mm});
            skLineSegment(sketch, "E79.6", {"start": v(-64.25, -74.25) * mm, "end": v(64.25, -74.25) * mm});
            skArc(sketch, "E79.7", {"start": v(-74.25, -64.25) * mm, "mid": v(-71.32, -71.32) * mm, "end": v(-64.25, -74.25) * mm});
            skCircle(sketch, "E79.9", {"center": v(60, -60) * mm, "radius": 4 * mm});
            skCircle(sketch, "E79.10", {"center": v(60, 60) * mm, "radius": 4 * mm});
            skCircle(sketch, "E79.11", {"center": v(-60, 60) * mm, "radius": 4 * mm});
            skCircle(sketch, "E79.12", {"center": v(-60, -60) * mm, "radius": 4 * mm});
            skArc(sketch, "E79.13", {"start": v(-54.26, -47.88) * mm, "mid": v(0, -60) * mm, "end": v(54.26, -47.88) * mm});
            skArc(sketch, "E79.14", {"start": v(-60, -38.83) * mm, "mid": v(-58.44, -44.2) * mm, "end": v(-54.26, -47.88) * mm});
            skLineSegment(sketch, "E79.15", {"start": v(-60, 38.83) * mm, "end": v(-60, -38.83) * mm});
            skArc(sketch, "E79.16", {"start": v(-54.26, 47.88) * mm, "mid": v(-58.44, 44.2) * mm, "end": v(-60, 38.83) * mm});
            skArc(sketch, "E79.17", {"start": v(54.26, 47.88) * mm, "mid": v(0, 60) * mm, "end": v(-54.26, 47.88) * mm});
            skArc(sketch, "E79.18", {"start": v(60, 38.83) * mm, "mid": v(58.44, 44.2) * mm, "end": v(54.26, 47.88) * mm});
            skLineSegment(sketch, "E79.19", {"start": v(60, 38.83) * mm, "end": v(60, -38.83) * mm});
            skArc(sketch, "E79.20", {"start": v(54.26, -47.88) * mm, "mid": v(58.44, -44.2) * mm, "end": v(60, -38.83) * mm});
            skLineSegment(sketch, "E80", {"start": v(0, 74.25) * mm, "end": v(0, 104.25) * mm, "construction": true});
            skCircle(sketch, "E81", {"center": v(0, 104.25) * mm, "radius": 6 * mm});
            skCircle(sketch, "E82.0", {"center": v(0, 104.25) * mm, "radius": 11 * mm});
            skLineSegment(sketch, "E83", {"start": v(-10.68, 106.87) * mm, "end": v(-15, 89.25) * mm});
            skLineSegment(sketch, "E84", {"start": v(-15, 89.25) * mm, "end": v(-30, 74.25) * mm});
            skLineSegment(sketch, "E85.MirrorCS", {"start": v(10.68, 106.87) * mm, "end": v(15, 89.25) * mm});
            skLineSegment(sketch, "E86.MirrorCS", {"start": v(15, 89.25) * mm, "end": v(30, 74.25) * mm});
            skSolve(sketch);
        }
        {
            var Q0;
            {var subQ0=sQuery(id+"F16.wireOp",EDGE,"E83");Q0=makeQuery(id+"F16.imprint","IMPRINT",FACE,{"disambiguationData":[TD([[makeQuery(id+"F16.imprint","IMPRINT",EDGE,{"derivedFrom":subQ0}),1.0]])]});}
            var Q1;
            Q1=makeQuery(id+"F16.imprint","IMPRINT",FACE,{"disambiguationData":[TD([[makeQuery(id+"F16.imprint","IMPRINT",EDGE,{"derivedFrom":sQuery(id+"F16.wireOp",EDGE,"E81")}),-1.0]])]});
            var Q2;
            {var subQ0=sQuery(id+"F4.wireOp",EDGE,"E36.filletArc");var subQ1=sQuery(id+"F4.wireOp",EDGE,"E35.filletArc");var subQ2=sQuery(id+"F4.wireOp",EDGE,"E34.filletArc");var subQ3=sQuery(id+"F4.wireOp",EDGE,"E33.filletArc");var subQ4=sQuery(id+"F4.wireOp",EDGE,"E27.0");var subQ5=sQuery(id+"F4.wireOp",EDGE,"E30");var subQ6=sQuery(id+"F4.wireOp",EDGE,"E28.0");var subQ7=sQuery(id+"F4.wireOp",EDGE,"E29");Q2=makeQuery(id+"F6.boolean.opBoolean","SPLIT",FACE,{"disambiguationData":[TD([makeQuery(id+"F5.opExtrude","SWEPT_FACE",FACE,{"disambiguationData":[OSD([subQ4])]})])],"derivedFrom":makeQuery(id+"F5.opExtrude","CAP_FACE",FACE,{"disambiguationData":[OSD([subQ4,subQ6,subQ7,subQ5,subQ3,subQ2,subQ1,subQ0,sQuery(id+"F4.wireOp",EDGE,"E41"),sQuery(id+"F4.wireOp",EDGE,"E42"),sQuery(id+"F4.wireOp",EDGE,"E43"),sQuery(id+"F4.wireOp",EDGE,"E45"),sQuery(id+"F4.wireOp",EDGE,"E46"),sQuery(id+"F4.wireOp",EDGE,"E47.filletArc"),sQuery(id+"F4.wireOp",EDGE,"E48.filletArc"),sQuery(id+"F4.wireOp",EDGE,"E49.filletArc"),sQuery(id+"F4.wireOp",EDGE,"E50.filletArc"),sQuery(id+"F4.wireOp",EDGE,"E51.filletArc"),sQuery(id+"F4.wireOp",EDGE,"E52.filletArc"),sQuery(id+"F4.wireOp",EDGE,"E53.0.MirrorCS"),sQuery(id+"F4.wireOp",EDGE,"E54.0.MirrorCS"),sQuery(id+"F4.wireOp",EDGE,"E55.0.MirrorCS"),sQuery(id+"F4.wireOp",EDGE,"E56.0.MirrorCS"),sQuery(id+"F4.wireOp",EDGE,"E57.0.MirrorCS"),sQuery(id+"F4.wireOp",EDGE,"E58.0.MirrorCS"),sQuery(id+"F4.wireOp",EDGE,"E59.0.MirrorCS"),sQuery(id+"F4.wireOp",EDGE,"E60.0.MirrorCS"),sQuery(id+"F4.wireOp",EDGE,"E61.0.MirrorCS"),sQuery(id+"F4.wireOp",EDGE,"E62.0.MirrorCS"),sQuery(id+"F4.wireOp",EDGE,"E63.0.MirrorCS")])],"isStart":true})});}
            var Q3;
            {var subQ0=sQuery(id+"F0.wireOp",EDGE,"E21.filletArc");var subQ1=sQuery(id+"F0.wireOp",EDGE,"E1.top");Q3=makeQuery(id+"F15.opFillet","BLEND_VERTEX",VERTEX,{"blendedFrom":[makeQuery(id+"F1.opExtrude","CAP_EDGE",EDGE,{"disambiguationData":[OSD([subQ1])],"isStart":false}),makeQuery(id+"F1.opExtrude","CAP_EDGE",EDGE,{"disambiguationData":[OSD([subQ0])],"isStart":false}),makeQuery(id+"F1.opExtrude","SWEPT_FACE",FACE,{"disambiguationData":[OSD([subQ1])]}),makeQuery(id+"F1.opExtrude","SWEPT_FACE",FACE,{"disambiguationData":[OSD([subQ0])]})],"blendedInto":[makeQuery(id+"F1.opExtrude","SWEPT_FACE",FACE,{"disambiguationData":[OSD([subQ1])]}),makeQuery(id+"F1.opExtrude","SWEPT_FACE",FACE,{"disambiguationData":[OSD([subQ0])]})]});}
            extrude(context, id + "F17", {"entities" : qUnion([Q0, Q1]), "endBound" : BoundingType.UP_TO_SURFACE, "depth" : 25 * mm, "endBoundEntityFace" : qUnion([Q2]), "endBoundEntityVertex" : qUnion([Q3]), "offsetDistance" : 25 * mm, "hasSecondDirection" : true, "secondDirectionOppositeDirection" : true, "secondDirectionDepth" : 10 * mm});
        }
        {
            var Q0;
            Q0=makeQuery(id+"F17.opExtrude","CAP_EDGE",EDGE,{"disambiguationData":[OSD([sQuery(id+"F16.wireOp",EDGE,"E79.0")])],"isStart":false});
            var Q1;
            Q1=makeQuery(id+"F1.opExtrude","CAP_EDGE",EDGE,{"disambiguationData":[OSD([sQuery(id+"F0.wireOp",EDGE,"E1.top")])],"isStart":true});
            var Q2;
            Q2=makeQuery(id+"F17.opExtrude","CAP_EDGE",EDGE,{"disambiguationData":[OSD([sQuery(id+"F16.wireOp",EDGE,"E81")])],"isStart":false});
            var Q3;
            Q3=makeQuery(id+"F17.opExtrude","CAP_EDGE",EDGE,{"disambiguationData":[OSD([sQuery(id+"F16.wireOp",EDGE,"E81")])],"isStart":true});
            var Q4;
            Q4=makeQuery(id+"F17.opExtrude","CAP_FACE",FACE,{"disambiguationData":[OSD([sQuery(id+"F16.wireOp",EDGE,"E79.0"),sQuery(id+"F16.wireOp",EDGE,"E81"),sQuery(id+"F16.wireOp",EDGE,"E82.0"),sQuery(id+"F16.wireOp",EDGE,"E83"),sQuery(id+"F16.wireOp",EDGE,"E84"),sQuery(id+"F16.wireOp",EDGE,"E85.MirrorCS"),sQuery(id+"F16.wireOp",EDGE,"E86.MirrorCS")])],"isStart":false});
            var Q5;
            Q5=makeQuery(id+"F17.opExtrude","CAP_FACE",FACE,{"disambiguationData":[OSD([sQuery(id+"F16.wireOp",EDGE,"E79.0"),sQuery(id+"F16.wireOp",EDGE,"E81"),sQuery(id+"F16.wireOp",EDGE,"E82.0"),sQuery(id+"F16.wireOp",EDGE,"E83"),sQuery(id+"F16.wireOp",EDGE,"E84"),sQuery(id+"F16.wireOp",EDGE,"E85.MirrorCS"),sQuery(id+"F16.wireOp",EDGE,"E86.MirrorCS")])],"isStart":true});
            fillet(context, id + "F18", {"entities" : qUnion([Q0, Q1, Q2, Q3, Q4, Q5]), "radius" : 1 * mm, "tangentPropagation" : true, "rho" : 0.5, "crossSection" : FilletCrossSection.CONIC, "allowEdgeOverflow" : false});
        }
        {
            var Q0;
            {var subQ0=sQuery(id+"F0.wireOp",EDGE,"E21.filletArc");var subQ1=sQuery(id+"F0.wireOp",EDGE,"E7");var subQ2=sQuery(id+"F0.wireOp",EDGE,"E6");var subQ3=sQuery(id+"F0.wireOp",EDGE,"E5");var subQ4=sQuery(id+"F0.wireOp",EDGE,"E4");var subQ5=sQuery(id+"F0.wireOp",EDGE,"E22.filletArc");var subQ6=sQuery(id+"F0.wireOp",EDGE,"E1.bottom");var subQ7=sQuery(id+"F0.wireOp",EDGE,"E1.right");var subQ8=sQuery(id+"F0.wireOp",EDGE,"E1.top");var subQ9=sQuery(id+"F0.wireOp",EDGE,"E1.left");var subQ10=sQuery(id+"F0.wireOp",EDGE,"E23.filletArc");var subQ11=sQuery(id+"F0.wireOp",EDGE,"E24.filletArc");Q0=makeQuery(id+"F2.boolean.opBoolean","SPLIT",FACE,{"disambiguationData":[TD([makeQuery(id+"F1.opExtrude","SWEPT_FACE",FACE,{"disambiguationData":[OSD([subQ6])]})])],"derivedFrom":makeQuery(id+"F1.opExtrude","CAP_FACE",FACE,{"disambiguationData":[OSD([subQ6,subQ8,subQ9,subQ7,subQ4,subQ3,subQ2,subQ1,subQ0,subQ5,subQ10,subQ11])],"isStart":true})});}
            var sketch = newSketch(context, id + "F19", { "sketchPlane" : qUnion([Q0])});
            skLineSegment(sketch, "E87.top", {"start": v(-60, 0) * mm, "end": v(-60, -60) * mm});
            skLineSegment(sketch, "E87.left", {"start": v(-60, -60) * mm, "end": v(-137.15, -60) * mm});
            skLineSegment(sketch, "E87.right", {"start": v(-60, 0) * mm, "end": v(-180, 0) * mm});
            skArc(sketch, "E88", {"start": v(-180, -95.23) * mm, "mid": v(-161.4, -121.52) * mm, "end": v(-137.15, -142.71) * mm});
            skPoint(sketch, "E89.end.orphan", {"position": v(76.59, -30) * mm});
            skPoint(sketch, "E90.orphan", {"position": v(60, -60) * mm});
            skLineSegment(sketch, "E91", {"start": v(-137.15, -60) * mm, "end": v(-137.15, -142.71) * mm});
            skPoint(sketch, "E92.orphan", {"position": v(73.25, -60) * mm});
            skLineSegment(sketch, "E93", {"start": v(-180, 0) * mm, "end": v(-180, -95.23) * mm});
            skPoint(sketch, "E94.start.orphan", {"position": v(-193.25, 0) * mm});
            skSolve(sketch);
        }
        {
            var Q0;
            Q0=makeQuery(id+"F19.imprint","IMPRINT",FACE,{"disambiguationData":[TD([[makeQuery(id+"F19.imprint","IMPRINT",EDGE,{"derivedFrom":sQuery(id+"F19.wireOp",EDGE,"E88")}),1.0]])]});
            var Q1;
            Q1=sQuery(id+"F19.wireOp",EDGE,"E87.right");
            revolve(context, id + "F20", {"surfaceOperationType" : NewSurfaceOperationType.NEW, "entities" : qUnion([Q0]), "axis" : qUnion([Q1]), "revolveType" : RevolveType.FULL});
        }
    });
